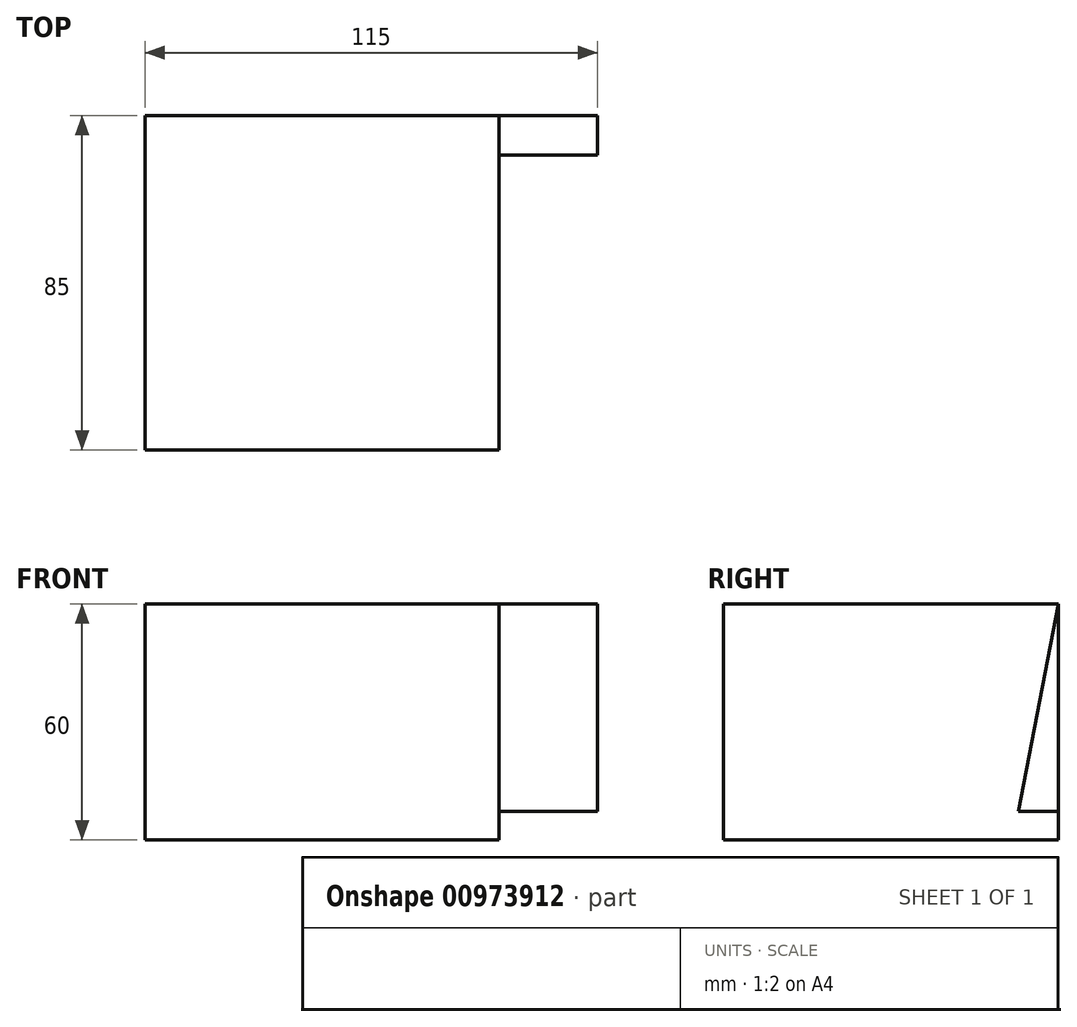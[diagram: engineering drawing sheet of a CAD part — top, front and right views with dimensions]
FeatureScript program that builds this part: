
annotation { "Feature Type Name" : "Feature", "Feature Type Description" : "" }
export const myFeature = defineFeature(function(context is Context, id is Id, definition is map)
    precondition{}
    {
        {
            var Q0;
            Q0=qCreatedBy(makeId("Front.planeOp"),FACE);
            var sketch = newSketch(context, id + "F0", { "sketchPlane" : qUnion([Q0])});
            skLineSegment(sketch, "E0.bottom", {"start": v(0, 0) * mm, "end": v(90, 0) * mm});
            skLineSegment(sketch, "E0.top", {"start": v(0, 60) * mm, "end": v(90, 60) * mm});
            skLineSegment(sketch, "E0.left", {"start": v(0, 0) * mm, "end": v(0, 60) * mm});
            skLineSegment(sketch, "E0.right", {"start": v(90, 0) * mm, "end": v(90, 60) * mm});
            skSolve(sketch);
        }
        {
            var Q0;
            Q0 = qSketchRegion(id + "F0", true);
            extrude(context, id + "F1", {"entities" : qUnion([Q0]), "depth" : 25 * mm, "offsetDistance" : 25 * mm});
        }
        {
            var Q0;
            Q0=makeQuery(id+"F1.opExtrude","CAP_FACE",FACE,{"disambiguationData":[OSD([sQuery(id+"F0.wireOp",EDGE,"E0.bottom"),sQuery(id+"F0.wireOp",EDGE,"E0.top"),sQuery(id+"F0.wireOp",EDGE,"E0.left"),sQuery(id+"F0.wireOp",EDGE,"E0.right")])],"isStart":false});
            extrude(context, id + "F2", {"entities" : qUnion([Q0]), "operationType" : NewBodyOperationType.ADD, "depth" : 60 * mm, "offsetDistance" : 25 * mm});
        }
        {
            var Q0;
            {var subQ0=sQuery(id+"F0.wireOp",EDGE,"E0.right");Q0=makeQuery(id+"F2.boolean.opBoolean","MERGE",FACE,{"derivedFrom":[makeQuery(id+"F1.opExtrude","SWEPT_FACE",FACE,{"disambiguationData":[OSD([subQ0])]}),makeQuery(id+"F2.opExtrude","SWEPT_FACE",FACE,{"disambiguationData":[OSD([subQ0])]})]});}
            var sketch = newSketch(context, id + "F3", { "sketchPlane" : qUnion([Q0])});
            skLineSegment(sketch, "E1", {"start": v(0, 60) * mm, "end": v(0, 7.24) * mm});
            skLineSegment(sketch, "E2", {"start": v(0, 7.24) * mm, "end": v(-10.07, 7.24) * mm});
            skLineSegment(sketch, "E3", {"start": v(-10.07, 7.24) * mm, "end": v(0, 60) * mm});
            skSolve(sketch);
        }
        {
            var Q0;
            Q0 = qSketchRegion(id + "F3", true);
            extrude(context, id + "F4", {"entities" : qUnion([Q0]), "operationType" : NewBodyOperationType.ADD, "depth" : 25 * mm, "offsetDistance" : 25 * mm});
        }
    });
